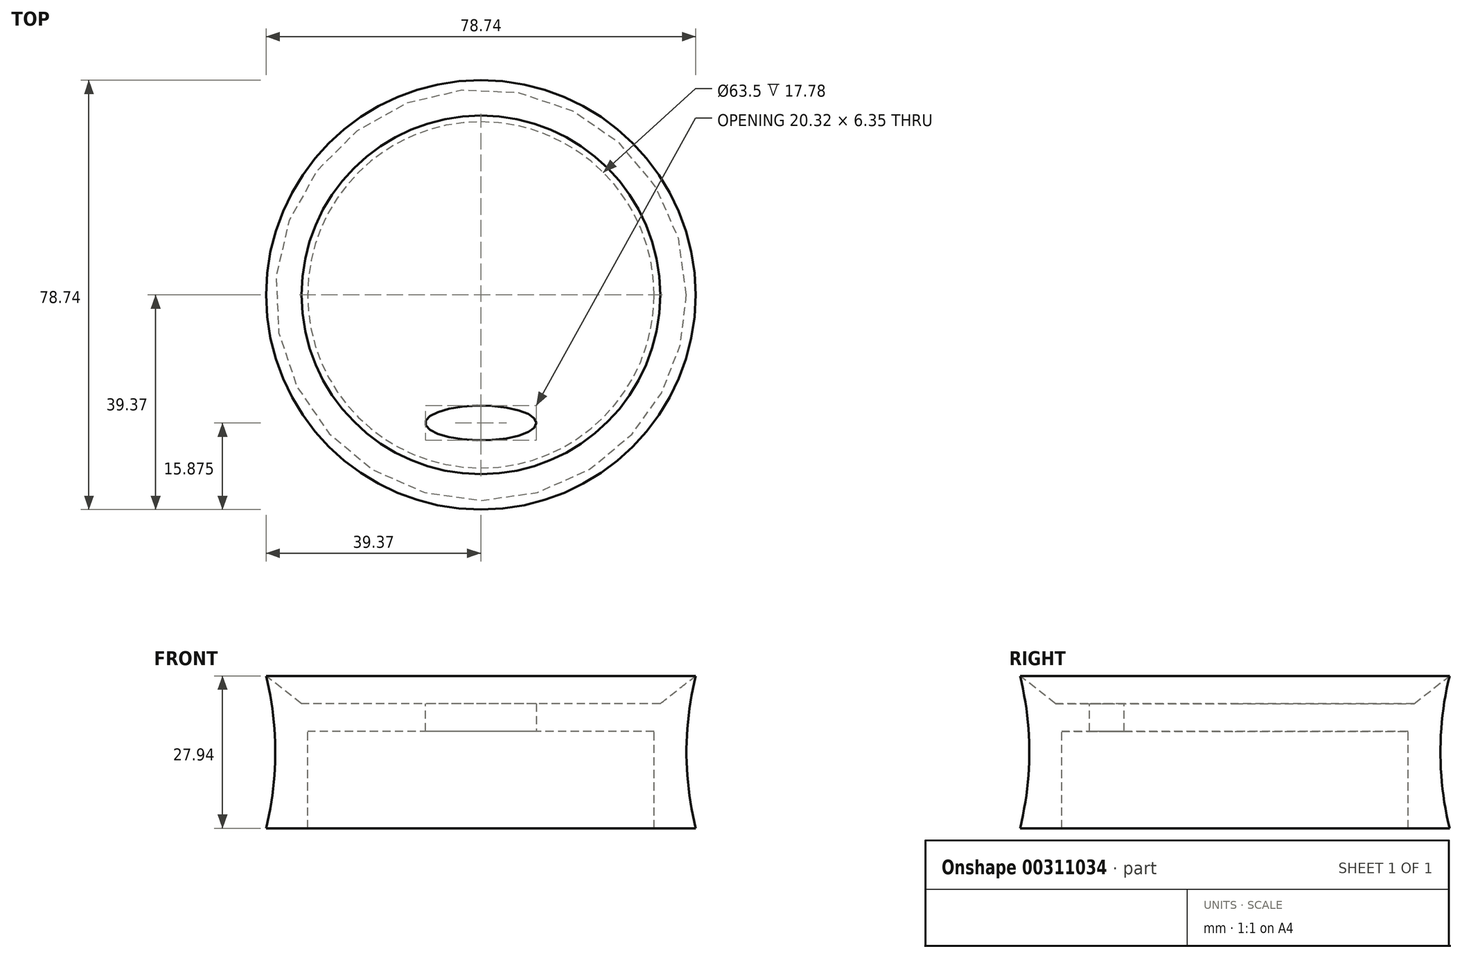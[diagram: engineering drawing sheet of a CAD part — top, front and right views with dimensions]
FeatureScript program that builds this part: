
annotation { "Feature Type Name" : "Feature", "Feature Type Description" : "" }
export const myFeature = defineFeature(function(context is Context, id is Id, definition is map)
    precondition{}
    {
        {
            var Q0;
            Q0=qCreatedBy(makeId("Front.planeOp"),FACE);
            var sketch = newSketch(context, id + "F0", { "sketchPlane" : qUnion([Q0])});
            skPoint(sketch, "E0.middle", {"position": v(0, 0) * mm});
            skArc(sketch, "E1", {"start": v(39.37, 15.7) * mm, "mid": v(37.7, 1.73) * mm, "end": v(39.37, -12.24) * mm});
            skLineSegment(sketch, "E2.bottom", {"start": v(0, -12.24) * mm, "end": v(39.37, -12.24) * mm});
            skLineSegment(sketch, "E3", {"start": v(32.89, 10.62) * mm, "end": v(39.37, 15.7) * mm});
            skLineSegment(sketch, "E4", {"start": v(31.75, 5.54) * mm, "end": v(31.75, -12.24) * mm});
            skLineSegment(sketch, "E5", {"start": v(0, 10.62) * mm, "end": v(0, -12.24) * mm});
            skLineSegment(sketch, "E6", {"start": v(31.75, 5.54) * mm, "end": v(0, 5.54) * mm});
            skLineSegment(sketch, "E7", {"start": v(0, 10.62) * mm, "end": v(32.89, 10.62) * mm});
            skSolve(sketch);
        }
        {
            var Q0;
            {var subQ2=sQuery(id+"F0.wireOp",EDGE,"E1");Q0=makeQuery(id+"F0.imprint","IMPRINT",FACE,{"disambiguationData":[TD([[makeQuery(id+"F0.imprint","IMPRINT",EDGE,{"derivedFrom":subQ2}),-1.0]])]});}
            var Q1;
            Q1=sQuery(id+"F0.wireOp",EDGE,"E5");
            revolve(context, id + "F1", {"entities" : qUnion([Q0]), "axis" : qUnion([Q1]), "revolveType" : RevolveType.FULL});
        }
        {
            var Q0;
            Q0=qCreatedBy(makeId("Top.planeOp"),FACE);
            var sketch = newSketch(context, id + "F2", { "sketchPlane" : qUnion([Q0])});
            skLineSegment(sketch, "E8", {"start": v(0, 0) * mm, "end": v(0, -23.5) * mm, "construction": true});
            skLineSegment(sketch, "E9", {"start": v(0, -23.5) * mm, "end": v(10.16, -23.5) * mm, "construction": true});
            skLineSegment(sketch, "E10", {"start": v(0, -23.5) * mm, "end": v(0, -20.32) * mm, "construction": true});
            skEllipse(sketch, "E11", {"center": v(0, -23.5) * mm, "majorRadius": 10.16 * mm, "minorRadius": 3.18 * mm, "majorAxis": v(1, 0)});
            skSolve(sketch);
        }
        {
            var Q0;
            Q0=makeQuery(id+"F2.imprint","IMPRINT",FACE,{"disambiguationData":[TD([[makeQuery(id+"F2.imprint","IMPRINT",EDGE,{"derivedFrom":sQuery(id+"F2.wireOp",EDGE,"E11")}),1.0]])]});
            extrude(context, id + "F3", {"entities" : qUnion([Q0]), "operationType" : NewBodyOperationType.REMOVE, "depth" : 99.82 * mm});
        }
    });
